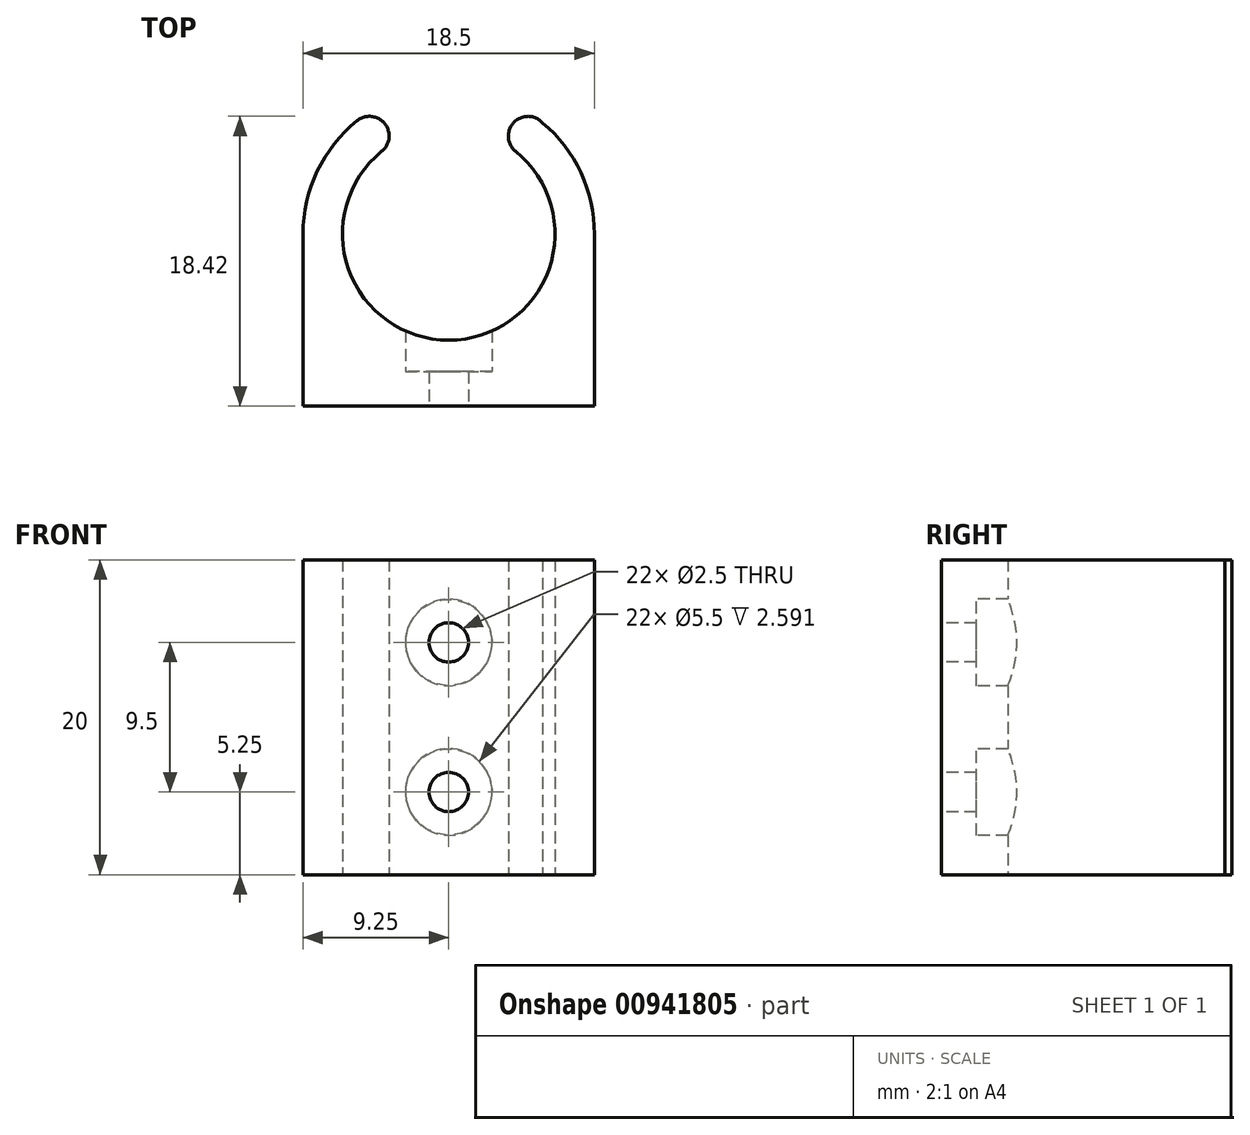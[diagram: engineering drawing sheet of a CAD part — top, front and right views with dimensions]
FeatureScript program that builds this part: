
annotation { "Feature Type Name" : "Feature", "Feature Type Description" : "" }
export const myFeature = defineFeature(function(context is Context, id is Id, definition is map)
    precondition{}
    {
        {
            var Q0;
            Q0=qCreatedBy(makeId("Top.planeOp"),FACE);
            var sketch = newSketch(context, id + "F0", { "sketchPlane" : qUnion([Q0])});
            skLineSegment(sketch, "E0.bottom", {"start": v(9.25, 9) * mm, "end": v(-9.25, 9) * mm, "construction": true});
            skLineSegment(sketch, "E0.top", {"start": v(9.25, -9) * mm, "end": v(-9.25, -9) * mm});
            skLineSegment(sketch, "E0.left", {"start": v(9.25, 9) * mm, "end": v(9.25, -9) * mm, "construction": true});
            skLineSegment(sketch, "E0.right", {"start": v(-9.25, 9) * mm, "end": v(-9.25, -9) * mm, "construction": true});
            skPoint(sketch, "E0.middle", {"position": v(0, 0) * mm});
            skLineSegment(sketch, "E1", {"start": v(-9.25, -4.8) * mm, "end": v(9.25, -4.8) * mm, "construction": true});
            skLineSegment(sketch, "E2", {"start": v(0, 7.2) * mm, "end": v(0, -7.2) * mm, "construction": true});
            skCircle(sketch, "E3", {"center": v(0, 1.95) * mm, "radius": 6.75 * mm, "construction": true});
            skLineSegment(sketch, "E4", {"start": v(-4.25, 7.2) * mm, "end": v(4.25, 7.2) * mm, "construction": true});
            skCircle(sketch, "E5.0", {"center": v(0, 1.95) * mm, "radius": 9.25 * mm, "construction": true});
            skLineSegment(sketch, "E6", {"start": v(9.25, 1.95) * mm, "end": v(9.25, -9) * mm});
            skLineSegment(sketch, "E7", {"start": v(-9.25, -9) * mm, "end": v(-9.25, 1.95) * mm});
            skArc(sketch, "E8", {"start": v(-4.25, 7.2) * mm, "mid": v(0, -4.8) * mm, "end": v(4.25, 7.2) * mm});
            skArc(sketch, "E9.0", {"start": v(-5.04, 8.17) * mm, "mid": v(0, -6.05) * mm, "end": v(5.04, 8.17) * mm, "construction": true});
            skArc(sketch, "E10", {"start": v(4.25, 7.2) * mm, "mid": v(4.13, 9.03) * mm, "end": v(5.97, 9) * mm});
            skArc(sketch, "E11", {"start": v(-4.25, 7.2) * mm, "mid": v(-4.07, 8.95) * mm, "end": v(-5.82, 9.14) * mm});
            skArc(sketch, "E12", {"start": v(-5.82, 9.14) * mm, "mid": v(-8.35, 5.93) * mm, "end": v(-9.25, 1.95) * mm});
            skArc(sketch, "E13", {"start": v(9.25, 1.95) * mm, "mid": v(8.39, 5.84) * mm, "end": v(5.97, 9) * mm});
            skSolve(sketch);
        }
        {
            var Q0;
            Q0=makeQuery(id+"F0.imprint","IMPRINT",FACE,{"disambiguationData":[TD([[makeQuery(id+"F0.imprint","IMPRINT",EDGE,{"derivedFrom":sQuery(id+"F0.wireOp",EDGE,"E0.top")}),-1.0]])]});
            extrude(context, id + "F1", {"entities" : qUnion([Q0]), "depth" : 20 * mm, "offsetDistance" : 25 * mm});
        }
        {
            var Q0;
            Q0=makeQuery(id+"F1.opExtrude","SWEPT_FACE",FACE,{"disambiguationData":[OSD([sQuery(id+"F0.wireOp",EDGE,"E0.top")])]});
            var sketch = newSketch(context, id + "F2", { "sketchPlane" : qUnion([Q0])});
            skLineSegment(sketch, "E14", {"start": v(0, 52.89) * mm, "end": v(0, -47.43) * mm, "construction": true});
            skLineSegment(sketch, "E15", {"start": v(-9.25, 20) * mm, "end": v(9.25, 20) * mm, "construction": true});
            skLineSegment(sketch, "E16", {"start": v(-9.25, 0) * mm, "end": v(9.25, 0) * mm, "construction": true});
            skLineSegment(sketch, "E17", {"start": v(-9.25, 10) * mm, "end": v(9.25, 10) * mm, "construction": true});
            skLineSegment(sketch, "E18", {"start": v(-15.96, 14.75) * mm, "end": v(17.9, 14.75) * mm, "construction": true});
            skLineSegment(sketch, "E19", {"start": v(-15.96, 5.25) * mm, "end": v(17.9, 5.25) * mm, "construction": true});
            skCircle(sketch, "E20", {"center": v(0, 14.75) * mm, "radius": 1.25 * mm});
            skCircle(sketch, "E21", {"center": v(0, 5.25) * mm, "radius": 1.25 * mm});
            skSolve(sketch);
        }
        {
            var Q0;
            Q0=makeQuery(id+"F2.imprint","IMPRINT",FACE,{"disambiguationData":[TD([[makeQuery(id+"F2.imprint","IMPRINT",EDGE,{"derivedFrom":sQuery(id+"F2.wireOp",EDGE,"E20")}),1.0]])]});
            var Q1;
            Q1=makeQuery(id+"F2.imprint","IMPRINT",FACE,{"disambiguationData":[TD([[makeQuery(id+"F2.imprint","IMPRINT",EDGE,{"derivedFrom":sQuery(id+"F2.wireOp",EDGE,"E21")}),1.0]])]});
            extrude(context, id + "F3", {"entities" : qUnion([Q0, Q1]), "operationType" : NewBodyOperationType.REMOVE, "oppositeDirection" : true, "depth" : 6 * mm, "offsetDistance" : 25 * mm});
        }
        {
            var Q0;
            Q0=makeQuery(id+"F1.opExtrude","SWEPT_FACE",FACE,{"disambiguationData":[OSD([sQuery(id+"F0.wireOp",EDGE,"E0.top")])]});
            cPlane(context, id + "F4", {"entities" : qUnion([Q0]), "cplaneType" : CPlaneType.OFFSET, "offset" : 2.2 * mm, "oppositeDirection" : true, "width" : 150 * mm, "height" : 150 * mm});
        }
        {
            var Q0;
            Q0=qCreatedBy(id+"F4.planeOp",FACE);
            var sketch = newSketch(context, id + "F5", { "sketchPlane" : qUnion([Q0])});
            skCircle(sketch, "E22.0", {"center": v(0, 14.75) * mm, "radius": 2.75 * mm});
            skCircle(sketch, "E23.0", {"center": v(0, 5.25) * mm, "radius": 2.75 * mm});
            skSolve(sketch);
        }
        {
            var Q0;
            Q0=makeQuery(id+"F5.imprint","IMPRINT",FACE,{"disambiguationData":[TD([[makeQuery(id+"F5.imprint","IMPRINT",EDGE,{"derivedFrom":sQuery(id+"F5.wireOp",EDGE,"E22.0")}),1.0]])]});
            var Q1;
            Q1=makeQuery(id+"F5.imprint","IMPRINT",FACE,{"disambiguationData":[TD([[makeQuery(id+"F5.imprint","IMPRINT",EDGE,{"derivedFrom":sQuery(id+"F5.wireOp",EDGE,"E23.0")}),1.0]])]});
            extrude(context, id + "F6", {"entities" : qUnion([Q0, Q1]), "operationType" : NewBodyOperationType.REMOVE, "oppositeDirection" : true, "depth" : 5 * mm, "offsetDistance" : 25 * mm});
        }
    });
